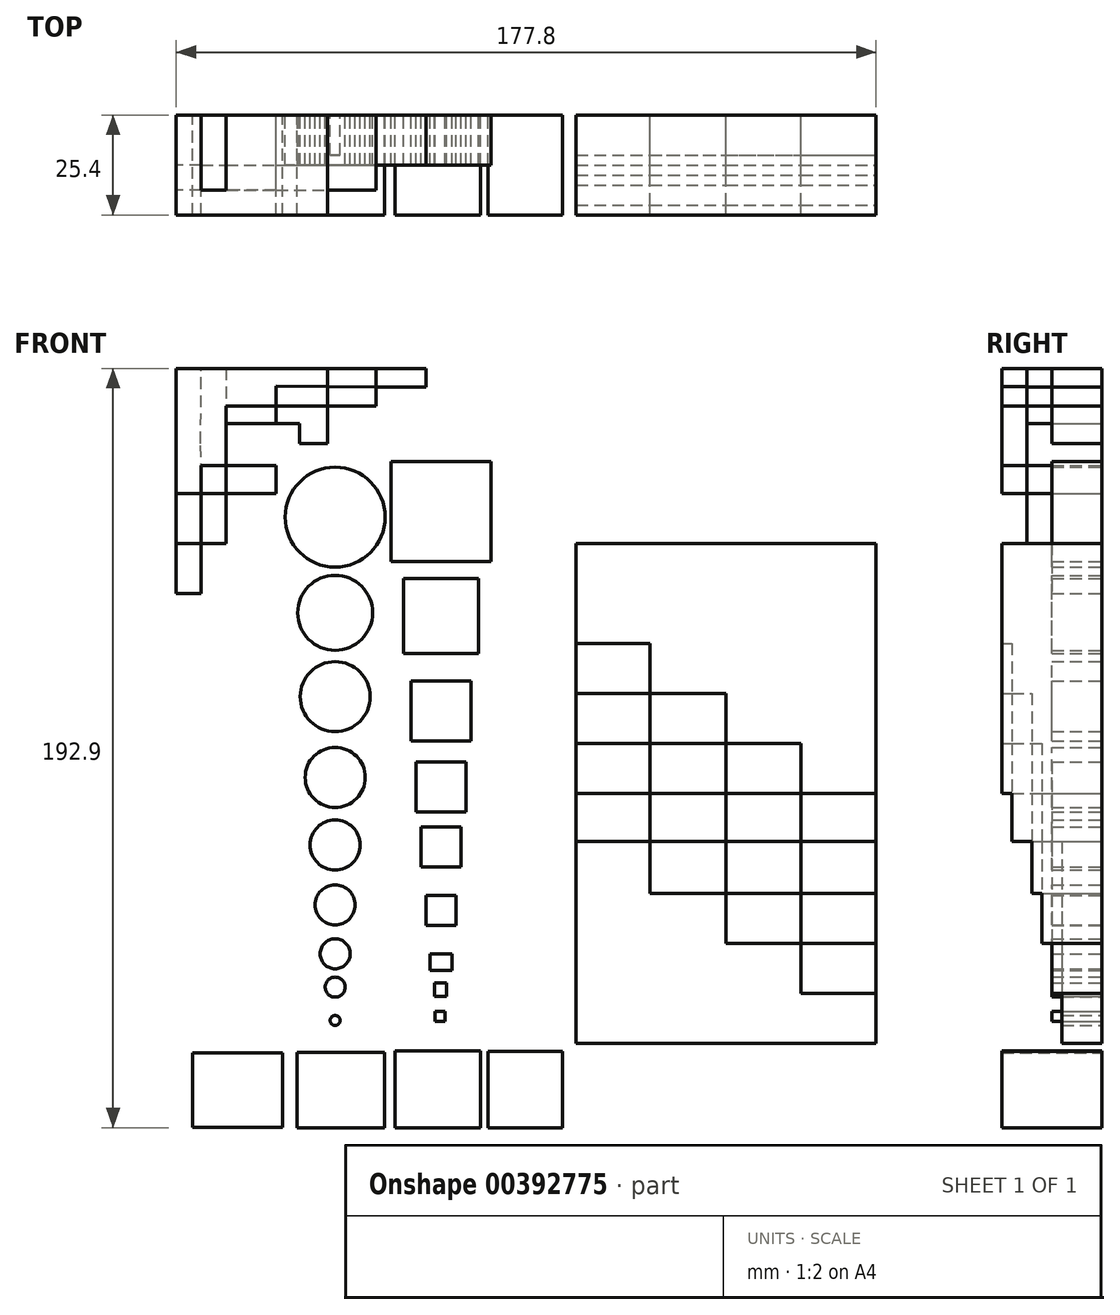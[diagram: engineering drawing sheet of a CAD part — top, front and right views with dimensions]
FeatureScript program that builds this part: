
annotation { "Feature Type Name" : "Feature", "Feature Type Description" : "" }
export const myFeature = defineFeature(function(context is Context, id is Id, definition is map)
    precondition{}
    {
        {
            var Q0;
            Q0=qCreatedBy(makeId("Front.planeOp"),FACE);
            var sketch = newSketch(context, id + "F0", { "sketchPlane" : qUnion([Q0])});
            skLineSegment(sketch, "E0.bottom", {"start": v(-139.7, 107.95) * mm, "end": v(139.7, 107.95) * mm});
            skLineSegment(sketch, "E0.top", {"start": v(-139.7, -107.95) * mm, "end": v(139.7, -107.95) * mm});
            skLineSegment(sketch, "E0.left", {"start": v(-139.7, 107.95) * mm, "end": v(-139.7, -107.95) * mm});
            skLineSegment(sketch, "E0.right", {"start": v(139.7, 107.95) * mm, "end": v(139.7, -107.95) * mm});
            skPoint(sketch, "E0.middle", {"position": v(0, 0) * mm});
            skLineSegment(sketch, "E1.bottom", {"start": v(-129.43, 76.2) * mm, "end": v(-104.03, 76.2) * mm});
            skLineSegment(sketch, "E1.top", {"start": v(-129.43, -76.2) * mm, "end": v(-104.03, -76.2) * mm});
            skLineSegment(sketch, "E1.left", {"start": v(-129.43, 76.2) * mm, "end": v(-129.43, -76.2) * mm});
            skLineSegment(sketch, "E1.right", {"start": v(-104.03, 76.2) * mm, "end": v(-104.03, -76.2) * mm});
            skLineSegment(sketch, "E2.bottom", {"start": v(-104.03, 76.2) * mm, "end": v(-27.83, 76.2) * mm});
            skLineSegment(sketch, "E2.top", {"start": v(-104.03, -76.2) * mm, "end": v(-27.83, -76.2) * mm});
            skLineSegment(sketch, "E2.right", {"start": v(-27.83, 76.2) * mm, "end": v(-27.83, -76.2) * mm});
            skLineSegment(sketch, "E3.bottom", {"start": v(-27.83, 76.2) * mm, "end": v(48.37, 76.2) * mm});
            skLineSegment(sketch, "E3.top", {"start": v(-27.83, -76.2) * mm, "end": v(48.37, -76.2) * mm});
            skLineSegment(sketch, "E3.right", {"start": v(48.37, 76.2) * mm, "end": v(48.37, -76.2) * mm});
            skPoint(sketch, "E4", {"position": v(-116.73, 76.2) * mm});
            skPoint(sketch, "E5", {"position": v(-116.73, -76.2) * mm});
            skLineSegment(sketch, "E6", {"start": v(-129.43, 0) * mm, "end": v(-116.57, 0) * mm});
            skPoint(sketch, "E6.startSnap0", {"position": v(-139.7, 0) * mm});
            skLineSegment(sketch, "E7", {"start": v(-116.73, -24.91) * mm, "end": v(-129.43, -24.91) * mm});
            skPoint(sketch, "E7.endSnap0", {"position": v(-129.43, 0) * mm});
            skLineSegment(sketch, "E8", {"start": v(-116.73, 50.8) * mm, "end": v(-129.43, 50.8) * mm});
            skLineSegment(sketch, "E9", {"start": v(-116.57, 25.4) * mm, "end": v(-129.43, 25.4) * mm});
            skLineSegment(sketch, "E10", {"start": v(-116.73, -50.8) * mm, "end": v(-129.43, -50.8) * mm});
            skPoint(sketch, "E11", {"position": v(-65.93, 76.2) * mm});
            skPoint(sketch, "E12", {"position": v(10.27, 76.2) * mm});
            skPoint(sketch, "E13", {"position": v(48.37, 0) * mm});
            skPoint(sketch, "E14", {"position": v(-65.93, -76.2) * mm});
            skPoint(sketch, "E15", {"position": v(10.27, -76.2) * mm});
            skPoint(sketch, "E16", {"position": v(10.27, 0) * mm});
            skPoint(sketch, "E17", {"position": v(-89.05, 76.2) * mm});
            skPoint(sketch, "E18", {"position": v(-62.1, 76.2) * mm});
            skPoint(sketch, "E19", {"position": v(-9.04, 76.2) * mm});
            skPoint(sketch, "E20", {"position": v(29.32, 76.2) * mm});
            skLineSegment(sketch, "E21.bottom", {"start": v(68.19, -99.33) * mm, "end": v(116.65, -99.33) * mm});
            skLineSegment(sketch, "E21.top", {"start": v(68.19, 67.86) * mm, "end": v(116.65, 67.86) * mm});
            skLineSegment(sketch, "E21.left", {"start": v(68.19, 67.86) * mm, "end": v(68.19, -99.33) * mm});
            skLineSegment(sketch, "E21.right", {"start": v(116.65, 67.86) * mm, "end": v(116.65, -99.33) * mm});
            skText(sketch, "E22", { "text": "Instructions", "fontName": "OpenSans-Regular.ttf"});
            skLineSegment(sketch, "E23", {"start": v(-123.08, 63.5) * mm, "end": v(-129.43, 63.5) * mm});
            skLineSegment(sketch, "E24", {"start": v(-129.43, 63.5) * mm, "end": v(-129.43, 50.8) * mm});
            skLineSegment(sketch, "E25", {"start": v(-129.43, 25.4) * mm, "end": v(-129.43, 38.1) * mm});
            skLineSegment(sketch, "E26", {"start": v(-129.43, 38.1) * mm, "end": v(-123.08, 38.1) * mm});
            skLineSegment(sketch, "E27", {"start": v(-123.08, 12.7) * mm, "end": v(-129.43, 12.7) * mm});
            skLineSegment(sketch, "E28", {"start": v(-129.43, 12.7) * mm, "end": v(-129.43, 0) * mm});
            skLineSegment(sketch, "E29", {"start": v(-123.08, -12.7) * mm, "end": v(-129.43, -12.7) * mm});
            skLineSegment(sketch, "E30", {"start": v(-129.43, -12.7) * mm, "end": v(-129.43, -24.91) * mm});
            skLineSegment(sketch, "E31", {"start": v(-123.08, -38.1) * mm, "end": v(-129.43, -38.1) * mm});
            skLineSegment(sketch, "E32", {"start": v(-129.43, -38.1) * mm, "end": v(-129.43, -50.8) * mm});
            skLineSegment(sketch, "E33", {"start": v(-123.08, -63.5) * mm, "end": v(-129.43, -63.5) * mm});
            skLineSegment(sketch, "E34", {"start": v(-129.43, -63.5) * mm, "end": v(-129.43, -76.2) * mm});
            skLineSegment(sketch, "E35.top", {"start": v(-27.83, 63.5) * mm, "end": v(48.37, 63.5) * mm});
            skLineSegment(sketch, "E35.left", {"start": v(-27.83, 76.2) * mm, "end": v(-27.83, 63.5) * mm});
            skLineSegment(sketch, "E35.right", {"start": v(48.37, 76.2) * mm, "end": v(48.37, 63.5) * mm});
            skLineSegment(sketch, "E36.bottom", {"start": v(-27.83, 63.5) * mm, "end": v(-9.04, 63.5) * mm});
            skLineSegment(sketch, "E36.top", {"start": v(-27.83, -76.2) * mm, "end": v(-9.04, -76.2) * mm});
            skLineSegment(sketch, "E36.left", {"start": v(-27.83, 63.5) * mm, "end": v(-27.83, -76.2) * mm});
            skLineSegment(sketch, "E36.right", {"start": v(-9.04, 63.5) * mm, "end": v(-9.04, -76.2) * mm});
            skLineSegment(sketch, "E37.bottom", {"start": v(-9.04, 63.5) * mm, "end": v(10.27, 63.5) * mm});
            skLineSegment(sketch, "E37.top", {"start": v(-9.04, -76.2) * mm, "end": v(10.27, -76.2) * mm});
            skLineSegment(sketch, "E37.right", {"start": v(10.27, 63.5) * mm, "end": v(10.27, -76.2) * mm});
            skLineSegment(sketch, "E38.bottom", {"start": v(10.27, 63.5) * mm, "end": v(29.32, 63.5) * mm});
            skLineSegment(sketch, "E38.top", {"start": v(10.27, -76.2) * mm, "end": v(29.32, -76.2) * mm});
            skLineSegment(sketch, "E38.right", {"start": v(29.32, 63.5) * mm, "end": v(29.32, -76.2) * mm});
            skLineSegment(sketch, "E39", {"start": v(-9.04, 76.2) * mm, "end": v(-9.04, 63.5) * mm});
            skLineSegment(sketch, "E40", {"start": v(10.27, 76.2) * mm, "end": v(10.27, 63.5) * mm});
            skLineSegment(sketch, "E41", {"start": v(29.32, 76.2) * mm, "end": v(29.32, 63.5) * mm});
            skPoint(sketch, "E42", {"position": v(-104.03, -63.5) * mm});
            skPoint(sketch, "E43", {"position": v(-104.03, -50.8) * mm});
            skPoint(sketch, "E44", {"position": v(-104.03, -38.1) * mm});
            skPoint(sketch, "E45", {"position": v(-104.03, -24.91) * mm});
            skPoint(sketch, "E46", {"position": v(-123.08, -12.7) * mm});
            skPoint(sketch, "E47", {"position": v(-104.03, -12.7) * mm});
            skPoint(sketch, "E48", {"position": v(-116.57, 0) * mm});
            skPoint(sketch, "E49", {"position": v(-104.03, 0) * mm});
            skPoint(sketch, "E50", {"position": v(-123.08, 12.7) * mm});
            skPoint(sketch, "E51", {"position": v(-104.03, 12.7) * mm});
            skPoint(sketch, "E52", {"position": v(-104.03, 25.4) * mm});
            skPoint(sketch, "E53", {"position": v(-104.03, 38.1) * mm});
            skPoint(sketch, "E54", {"position": v(-104.03, 50.8) * mm});
            skPoint(sketch, "E55", {"position": v(-104.03, 63.5) * mm});
            skPoint(sketch, "E56", {"position": v(-27.83, 50.8) * mm});
            skPoint(sketch, "E57", {"position": v(-27.83, 38.1) * mm});
            skPoint(sketch, "E58", {"position": v(-27.83, 25.4) * mm});
            skPoint(sketch, "E59", {"position": v(-27.83, 12.7) * mm});
            skPoint(sketch, "E60", {"position": v(-27.83, 0) * mm});
            skPoint(sketch, "E61", {"position": v(-27.83, -12.7) * mm});
            skPoint(sketch, "E62", {"position": v(-27.83, -24.91) * mm});
            skPoint(sketch, "E63", {"position": v(-27.83, -38.1) * mm});
            skPoint(sketch, "E64", {"position": v(-27.83, -50.8) * mm});
            skPoint(sketch, "E65", {"position": v(-27.83, -63.5) * mm});
            skPoint(sketch, "E66", {"position": v(-9.04, 50.8) * mm});
            skPoint(sketch, "E67", {"position": v(-9.04, 38.1) * mm});
            skPoint(sketch, "E68", {"position": v(10.27, 38.1) * mm});
            skPoint(sketch, "E69", {"position": v(29.32, 38.1) * mm});
            skPoint(sketch, "E70", {"position": v(48.37, 38.1) * mm});
            skPoint(sketch, "E71", {"position": v(29.32, 50.8) * mm});
            skPoint(sketch, "E72", {"position": v(10.27, 50.8) * mm});
            skPoint(sketch, "E73", {"position": v(48.37, 50.8) * mm});
            skPoint(sketch, "E74", {"position": v(-9.04, 25.4) * mm});
            skPoint(sketch, "E75", {"position": v(10.27, 25.4) * mm});
            skPoint(sketch, "E76", {"position": v(29.32, 25.4) * mm});
            skPoint(sketch, "E77", {"position": v(48.37, 25.4) * mm});
            skPoint(sketch, "E78", {"position": v(-9.04, 12.7) * mm});
            skPoint(sketch, "E79", {"position": v(10.27, 12.7) * mm});
            skPoint(sketch, "E80", {"position": v(-8.78, 0) * mm});
            skPoint(sketch, "E81", {"position": v(-9.04, -12.7) * mm});
            skPoint(sketch, "E82", {"position": v(-9.04, -24.91) * mm});
            skPoint(sketch, "E83", {"position": v(-9.04, -38.1) * mm});
            skPoint(sketch, "E84", {"position": v(-9.04, -50.8) * mm});
            skPoint(sketch, "E85", {"position": v(-9.04, -63.5) * mm});
            skPoint(sketch, "E86", {"position": v(10.27, -63.5) * mm});
            skPoint(sketch, "E87", {"position": v(29.32, -63.5) * mm});
            skPoint(sketch, "E88", {"position": v(48.37, -63.5) * mm});
            skPoint(sketch, "E89", {"position": v(48.37, -50.8) * mm});
            skPoint(sketch, "E90", {"position": v(29.32, -50.8) * mm});
            skPoint(sketch, "E91", {"position": v(10.27, -50.8) * mm});
            skPoint(sketch, "E92", {"position": v(10.27, -38.1) * mm});
            skPoint(sketch, "E93", {"position": v(29.32, -38.1) * mm});
            skPoint(sketch, "E94", {"position": v(48.37, -38.1) * mm});
            skPoint(sketch, "E95", {"position": v(48.37, -24.91) * mm});
            skPoint(sketch, "E96", {"position": v(29.32, -24.91) * mm});
            skPoint(sketch, "E97", {"position": v(10.27, -24.91) * mm});
            skPoint(sketch, "E98", {"position": v(10.27, -12.7) * mm});
            skPoint(sketch, "E99", {"position": v(29.32, -12.7) * mm});
            skPoint(sketch, "E100", {"position": v(48.37, -12.7) * mm});
            skPoint(sketch, "E101", {"position": v(48.37, 12.7) * mm});
            skPoint(sketch, "E102", {"position": v(29.32, 12.7) * mm});
            skPoint(sketch, "E103", {"position": v(29.32, 0) * mm});
            skCircle(sketch, "E104", {"center": v(-89.05, 57.46) * mm, "radius": 12.7 * mm});
            skCircle(sketch, "E105", {"center": v(-89.05, 33.17) * mm, "radius": 9.53 * mm});
            skCircle(sketch, "E106", {"center": v(-89.05, -8.65) * mm, "radius": 7.62 * mm});
            skCircle(sketch, "E107", {"center": v(-89.05, -25.83) * mm, "radius": 6.35 * mm});
            skCircle(sketch, "E108", {"center": v(-89.05, -41.03) * mm, "radius": 5.08 * mm});
            skCircle(sketch, "E109", {"center": v(-89.05, -53.47) * mm, "radius": 3.81 * mm});
            skCircle(sketch, "E110", {"center": v(-89.05, -61.94) * mm, "radius": 2.54 * mm});
            skCircle(sketch, "E111", {"center": v(-89.05, -70.41) * mm, "radius": 1.27 * mm});
            skCircle(sketch, "E112", {"center": v(-89.05, 11.86) * mm, "radius": 8.9 * mm});
            skLineSegment(sketch, "E113", {"start": v(-27.83, -24.91) * mm, "end": v(-9.04, -24.91) * mm});
            skLineSegment(sketch, "E114", {"start": v(-9.04, -38.1) * mm, "end": v(10.27, -38.1) * mm});
            skLineSegment(sketch, "E115", {"start": v(10.27, -50.8) * mm, "end": v(29.32, -50.8) * mm});
            skLineSegment(sketch, "E116", {"start": v(29.32, -63.5) * mm, "end": v(48.37, -63.5) * mm});
            skLineSegment(sketch, "E117.bottom", {"start": v(-64.92, -53.52) * mm, "end": v(-59.3, -53.52) * mm});
            skLineSegment(sketch, "E117.top", {"start": v(-64.92, -57.7) * mm, "end": v(-59.3, -57.7) * mm});
            skLineSegment(sketch, "E117.left", {"start": v(-64.92, -53.52) * mm, "end": v(-64.92, -57.7) * mm});
            skLineSegment(sketch, "E117.right", {"start": v(-59.3, -53.52) * mm, "end": v(-59.3, -57.7) * mm});
            skPoint(sketch, "E117.middle", {"position": v(-62.1, -55.6) * mm});
            skLineSegment(sketch, "E118.bottom", {"start": v(-63.7, -68.11) * mm, "end": v(-61.16, -68.11) * mm});
            skLineSegment(sketch, "E118.top", {"start": v(-63.7, -70.65) * mm, "end": v(-61.16, -70.65) * mm});
            skLineSegment(sketch, "E118.left", {"start": v(-63.7, -68.11) * mm, "end": v(-63.7, -70.65) * mm});
            skLineSegment(sketch, "E118.right", {"start": v(-61.16, -68.11) * mm, "end": v(-61.16, -70.65) * mm});
            skPoint(sketch, "E118.middle", {"position": v(-62.43, -69.38) * mm});
            skLineSegment(sketch, "E119.bottom", {"start": v(48.37, -76.2) * mm, "end": v(-129.43, -76.2) * mm});
            skLineSegment(sketch, "E119.top", {"start": v(48.37, -100.6) * mm, "end": v(-129.43, -100.6) * mm});
            skLineSegment(sketch, "E119.left", {"start": v(48.37, -76.2) * mm, "end": v(48.37, -100.6) * mm});
            skLineSegment(sketch, "E119.right", {"start": v(-129.43, -76.2) * mm, "end": v(-129.43, -100.6) * mm});
            skLineSegment(sketch, "E120.top", {"start": v(-27.83, -100.6) * mm, "end": v(-9.04, -100.6) * mm});
            skLineSegment(sketch, "E120.left", {"start": v(-27.83, -76.2) * mm, "end": v(-27.83, -100.6) * mm});
            skLineSegment(sketch, "E120.right", {"start": v(-9.04, -76.2) * mm, "end": v(-9.04, -100.6) * mm});
            skLineSegment(sketch, "E121.top", {"start": v(10.27, -100.6) * mm, "end": v(29.32, -100.6) * mm});
            skLineSegment(sketch, "E121.left", {"start": v(10.27, -76.2) * mm, "end": v(10.27, -100.6) * mm});
            skLineSegment(sketch, "E121.right", {"start": v(29.32, -76.2) * mm, "end": v(29.32, -100.6) * mm});
            skLineSegment(sketch, "E122", {"start": v(-27.83, 25.4) * mm, "end": v(-9.04, 25.4) * mm});
            skLineSegment(sketch, "E123", {"start": v(-9.04, 12.7) * mm, "end": v(10.27, 12.7) * mm});
            skLineSegment(sketch, "E124", {"start": v(10.27, 0) * mm, "end": v(29.32, 0) * mm});
            skLineSegment(sketch, "E125", {"start": v(29.32, -12.7) * mm, "end": v(48.37, -12.7) * mm});
            skLineSegment(sketch, "E126", {"start": v(-27.83, 12.7) * mm, "end": v(-9.04, 12.7) * mm});
            skLineSegment(sketch, "E127", {"start": v(-8.78, 0) * mm, "end": v(10.27, 0) * mm});
            skLineSegment(sketch, "E128", {"start": v(10.27, -12.7) * mm, "end": v(29.32, -12.7) * mm});
            skLineSegment(sketch, "E129", {"start": v(-27.83, 0) * mm, "end": v(-8.78, 0) * mm});
            skLineSegment(sketch, "E130", {"start": v(-27.83, -12.7) * mm, "end": v(-9.04, -12.7) * mm});
            skLineSegment(sketch, "E131", {"start": v(-9.04, -12.7) * mm, "end": v(10.27, -12.7) * mm});
            skLineSegment(sketch, "E132", {"start": v(10.27, -38.1) * mm, "end": v(29.32, -38.1) * mm});
            skLineSegment(sketch, "E133", {"start": v(29.32, -38.1) * mm, "end": v(48.37, -38.1) * mm});
            skLineSegment(sketch, "E134", {"start": v(29.32, -50.8) * mm, "end": v(48.37, -50.8) * mm});
            skLineSegment(sketch, "E135", {"start": v(-9.04, -24.91) * mm, "end": v(10.27, -24.91) * mm});
            skLineSegment(sketch, "E136", {"start": v(10.27, -24.91) * mm, "end": v(29.32, -24.91) * mm});
            skLineSegment(sketch, "E137", {"start": v(29.32, -24.91) * mm, "end": v(48.37, -24.91) * mm});
            skLineSegment(sketch, "E138", {"start": v(-27.83, 50.8) * mm, "end": v(48.37, 50.8) * mm});
            skLineSegment(sketch, "E139.bottom", {"start": v(-49.4, 46.22) * mm, "end": v(-74.8, 46.22) * mm});
            skLineSegment(sketch, "E139.top", {"start": v(-49.4, 71.62) * mm, "end": v(-74.8, 71.62) * mm});
            skLineSegment(sketch, "E139.left", {"start": v(-49.4, 46.22) * mm, "end": v(-49.4, 71.62) * mm});
            skLineSegment(sketch, "E139.right", {"start": v(-74.8, 46.22) * mm, "end": v(-74.8, 71.62) * mm});
            skPoint(sketch, "E139.middle", {"position": v(-62.1, 58.92) * mm});
            skLineSegment(sketch, "E140.bottom", {"start": v(-52.58, 22.78) * mm, "end": v(-71.63, 22.78) * mm});
            skLineSegment(sketch, "E140.top", {"start": v(-52.58, 41.83) * mm, "end": v(-71.63, 41.83) * mm});
            skLineSegment(sketch, "E140.left", {"start": v(-52.58, 22.78) * mm, "end": v(-52.58, 41.83) * mm});
            skLineSegment(sketch, "E140.right", {"start": v(-71.63, 22.78) * mm, "end": v(-71.63, 41.83) * mm});
            skPoint(sketch, "E140.middle", {"position": v(-62.1, 32.3) * mm});
            skLineSegment(sketch, "E141.bottom", {"start": v(-54.49, 0.58) * mm, "end": v(-69.73, 0.58) * mm});
            skLineSegment(sketch, "E141.top", {"start": v(-54.49, 15.82) * mm, "end": v(-69.73, 15.82) * mm});
            skLineSegment(sketch, "E141.left", {"start": v(-54.49, 0.58) * mm, "end": v(-54.49, 15.82) * mm});
            skLineSegment(sketch, "E141.right", {"start": v(-69.73, 0.58) * mm, "end": v(-69.73, 15.82) * mm});
            skPoint(sketch, "E141.middle", {"position": v(-62.1, 8.2) * mm});
            skLineSegment(sketch, "E142.bottom", {"start": v(-65.92, -38.58) * mm, "end": v(-58.3, -38.58) * mm});
            skLineSegment(sketch, "E142.top", {"start": v(-65.92, -46.2) * mm, "end": v(-58.3, -46.2) * mm});
            skLineSegment(sketch, "E142.left", {"start": v(-65.92, -38.58) * mm, "end": v(-65.92, -46.2) * mm});
            skLineSegment(sketch, "E142.right", {"start": v(-58.3, -38.58) * mm, "end": v(-58.3, -46.2) * mm});
            skPoint(sketch, "E142.middle", {"position": v(-62.1, -42.4) * mm});
            skLineSegment(sketch, "E143.bottom", {"start": v(-67.19, -21.2) * mm, "end": v(-57.03, -21.2) * mm});
            skLineSegment(sketch, "E143.top", {"start": v(-67.19, -31.35) * mm, "end": v(-57.03, -31.35) * mm});
            skLineSegment(sketch, "E143.left", {"start": v(-67.19, -21.2) * mm, "end": v(-67.19, -31.35) * mm});
            skLineSegment(sketch, "E143.right", {"start": v(-57.03, -21.2) * mm, "end": v(-57.03, -31.35) * mm});
            skPoint(sketch, "E143.middle", {"position": v(-62.1, -26.27) * mm});
            skLineSegment(sketch, "E144.bottom", {"start": v(-68.46, -4.78) * mm, "end": v(-55.76, -4.78) * mm});
            skLineSegment(sketch, "E144.top", {"start": v(-68.46, -17.48) * mm, "end": v(-55.76, -17.48) * mm});
            skLineSegment(sketch, "E144.left", {"start": v(-68.46, -4.78) * mm, "end": v(-68.46, -17.48) * mm});
            skLineSegment(sketch, "E144.right", {"start": v(-55.76, -4.78) * mm, "end": v(-55.76, -17.48) * mm});
            skPoint(sketch, "E144.middle", {"position": v(-62.1, -11.13) * mm});
            skLineSegment(sketch, "E145.bottom", {"start": v(-60.78, -64.35) * mm, "end": v(-63.79, -64.35) * mm});
            skLineSegment(sketch, "E145.top", {"start": v(-60.78, -60.9) * mm, "end": v(-63.79, -60.9) * mm});
            skLineSegment(sketch, "E145.left", {"start": v(-60.78, -64.35) * mm, "end": v(-60.78, -60.9) * mm});
            skLineSegment(sketch, "E145.right", {"start": v(-63.79, -64.35) * mm, "end": v(-63.79, -60.9) * mm});
            skPoint(sketch, "E145.middle", {"position": v(-62.28, -62.62) * mm});
            skLineSegment(sketch, "E146.bottom", {"start": v(-129.43, 76.2) * mm, "end": v(48.37, 76.2) * mm});
            skLineSegment(sketch, "E146.top", {"start": v(-129.43, 95.25) * mm, "end": v(48.37, 95.25) * mm});
            skLineSegment(sketch, "E146.left", {"start": v(-129.43, 76.2) * mm, "end": v(-129.43, 95.25) * mm});
            skLineSegment(sketch, "E146.right", {"start": v(48.37, 76.2) * mm, "end": v(48.37, 95.25) * mm});
            skPoint(sketch, "E147", {"position": v(-104.03, 95.25) * mm});
            skPoint(sketch, "E148", {"position": v(-89.05, 95.25) * mm});
            skPoint(sketch, "E149", {"position": v(-27.83, 95.25) * mm});
            skPoint(sketch, "E150", {"position": v(-9.04, 95.25) * mm});
            skPoint(sketch, "E151", {"position": v(10.27, 95.25) * mm});
            skPoint(sketch, "E152", {"position": v(29.32, 95.25) * mm});
            skPoint(sketch, "E153", {"position": v(-46.03, 95.25) * mm});
            skPoint(sketch, "E154", {"position": v(-116.73, 95.25) * mm});
            skPoint(sketch, "E155", {"position": v(-129.43, 85.72) * mm});
            skPoint(sketch, "E156", {"position": v(48.37, 85.72) * mm});
            skLineSegment(sketch, "E157", {"start": v(-104.03, 95.25) * mm, "end": v(-104.03, 85.72) * mm});
            skPoint(sketch, "E158", {"position": v(-76.14, 95.25) * mm});
            skPoint(sketch, "E159", {"position": v(-210.78, 24.73) * mm});
            skLineSegment(sketch, "E160.1.0.0", {"start": v(-78.63, 95.25) * mm, "end": v(-78.63, 85.72) * mm});
            skLineSegment(sketch, "E160.2.0.0", {"start": v(-53.23, 95.25) * mm, "end": v(-53.23, 85.72) * mm});
            skLineSegment(sketch, "E160.3.0.0", {"start": v(-27.83, 95.25) * mm, "end": v(-27.83, 85.72) * mm});
            skLineSegment(sketch, "E160.4.0.0", {"start": v(-2.43, 95.25) * mm, "end": v(-2.43, 85.72) * mm});
            skLineSegment(sketch, "E160.5.0.0", {"start": v(22.97, 95.25) * mm, "end": v(22.97, 85.72) * mm});
            skLineSegment(sketch, "E160.direction1", {"start": v(-104.03, 85.72) * mm, "end": v(-78.63, 85.72) * mm, "construction": true});
            skLineSegment(sketch, "E161", {"start": v(-129.43, 85.72) * mm, "end": v(-78.63, 85.72) * mm});
            skLineSegment(sketch, "E162", {"start": v(-123.08, 63.5) * mm, "end": v(-104.03, 63.5) * mm});
            skLineSegment(sketch, "E163", {"start": v(-103.97, 75.58) * mm, "end": v(-104.03, 85.72) * mm});
            skLineSegment(sketch, "E164", {"start": v(-116.73, 95.25) * mm, "end": v(-116.73, 63.5) * mm});
            skPoint(sketch, "E165", {"position": v(-123.13, 95.25) * mm});
            skPoint(sketch, "E166", {"position": v(-110.36, 95.25) * mm});
            skPoint(sketch, "E167", {"position": v(-96.53, 95.25) * mm});
            skPoint(sketch, "E168", {"position": v(-123.2, 76.2) * mm});
            skPoint(sketch, "E169", {"position": v(-110.3, 76.2) * mm});
            skPoint(sketch, "E170", {"position": v(-129.43, 90.76) * mm});
            skPoint(sketch, "E171", {"position": v(-129.43, 81.3) * mm});
            skLineSegment(sketch, "E172", {"start": v(-129.43, 90.76) * mm, "end": v(-104.03, 90.76) * mm});
            skLineSegment(sketch, "E173", {"start": v(-104, 81.3) * mm, "end": v(-129.43, 81.3) * mm});
            skLineSegment(sketch, "E174", {"start": v(-123.2, 76.2) * mm, "end": v(-123.13, 95.25) * mm});
            skLineSegment(sketch, "E175", {"start": v(-123.08, 63.5) * mm, "end": v(-123.2, 76.2) * mm});
            skLineSegment(sketch, "E176", {"start": v(-110.36, 95.25) * mm, "end": v(-110.36, 63.5) * mm});
            skLineSegment(sketch, "E177", {"start": v(-116.73, 50.8) * mm, "end": v(-116.73, 63.5) * mm});
            skLineSegment(sketch, "E178", {"start": v(-123.08, 63.5) * mm, "end": v(-123.08, 38.1) * mm});
            skLineSegment(sketch, "E179", {"start": v(-104.03, 90.76) * mm, "end": v(-65.99, 90.49) * mm});
            skPoint(sketch, "E179.endSnap0", {"position": v(-78.63, 90.49) * mm});
            skLineSegment(sketch, "E180", {"start": v(-91, 95.25) * mm, "end": v(-91, 85.72) * mm});
            skLineSegment(sketch, "E181", {"start": v(-98, 95.25) * mm, "end": v(-98, 85.72) * mm});
            skLineSegment(sketch, "E182", {"start": v(-98.14, 76.2) * mm, "end": v(-98, 85.72) * mm});
            skLineSegment(sketch, "E183", {"start": v(-104, 81.3) * mm, "end": v(-98, 81.27) * mm});
            skLineSegment(sketch, "E184", {"start": v(-65.99, 90.49) * mm, "end": v(-65.99, 95.25) * mm});
            skLineSegment(sketch, "E185", {"start": v(-84.93, 95.25) * mm, "end": v(-84.93, 85.72) * mm});
            skLineSegment(sketch, "E186", {"start": v(-129.43, 70.6) * mm, "end": v(-104.03, 70.6) * mm});
            skLineSegment(sketch, "E187", {"start": v(-129.43, 57.15) * mm, "end": v(-116.73, 57.15) * mm});
            skLineSegment(sketch, "E188", {"start": v(-129.43, 45.08) * mm, "end": v(-123.08, 45.08) * mm});
            skLineSegment(sketch, "E189", {"start": v(-72.6, 95.25) * mm, "end": v(-72.6, 90.53) * mm});
            skLineSegment(sketch, "E190", {"start": v(-91, 85.72) * mm, "end": v(-91, 76.2) * mm});
            skLineSegment(sketch, "E191", {"start": v(-98, 81.27) * mm, "end": v(-91, 81.27) * mm});
            skLineSegment(sketch, "E192.bottom", {"start": v(-125.23, -78.61) * mm, "end": v(-102.43, -78.61) * mm});
            skLineSegment(sketch, "E192.top", {"start": v(-125.23, -97.54) * mm, "end": v(-102.43, -97.54) * mm});
            skLineSegment(sketch, "E192.left", {"start": v(-125.23, -78.61) * mm, "end": v(-125.23, -97.54) * mm});
            skLineSegment(sketch, "E192.right", {"start": v(-102.43, -78.61) * mm, "end": v(-102.43, -97.54) * mm});
            skLineSegment(sketch, "E193.bottom", {"start": v(-98.75, -78.48) * mm, "end": v(-76.5, -78.48) * mm});
            skLineSegment(sketch, "E193.top", {"start": v(-98.75, -97.65) * mm, "end": v(-76.5, -97.65) * mm});
            skLineSegment(sketch, "E193.left", {"start": v(-98.75, -78.48) * mm, "end": v(-98.75, -97.65) * mm});
            skLineSegment(sketch, "E193.right", {"start": v(-76.5, -78.48) * mm, "end": v(-76.5, -97.65) * mm});
            skLineSegment(sketch, "E194.bottom", {"start": v(-73.79, -78.12) * mm, "end": v(-52.09, -78.12) * mm});
            skLineSegment(sketch, "E194.top", {"start": v(-73.79, -97.65) * mm, "end": v(-52.09, -97.65) * mm});
            skLineSegment(sketch, "E194.left", {"start": v(-73.79, -78.12) * mm, "end": v(-73.79, -97.65) * mm});
            skLineSegment(sketch, "E194.right", {"start": v(-52.09, -78.12) * mm, "end": v(-52.09, -97.65) * mm});
            skLineSegment(sketch, "E195.bottom", {"start": v(-50.28, -78.3) * mm, "end": v(-31.29, -78.3) * mm});
            skLineSegment(sketch, "E195.top", {"start": v(-50.28, -97.65) * mm, "end": v(-31.29, -97.65) * mm});
            skLineSegment(sketch, "E195.left", {"start": v(-50.28, -78.3) * mm, "end": v(-50.28, -97.65) * mm});
            skLineSegment(sketch, "E195.right", {"start": v(-31.29, -78.3) * mm, "end": v(-31.29, -97.65) * mm});
            skPoint(sketch, "E196", {"position": v(-22.97, -18.6) * mm});
            skPoint(sketch, "E197", {"position": v(-15.04, -19.37) * mm});
            skPoint(sketch, "E198", {"position": v(-2.5, -16.82) * mm});
            skPoint(sketch, "E199", {"position": v(4.15, -19.89) * mm});
            skPoint(sketch, "E200", {"position": v(20, -16.56) * mm});
            skPoint(sketch, "E201", {"position": v(14.89, -20.4) * mm});
            skPoint(sketch, "E202", {"position": v(40.98, -17.33) * mm});
            skPoint(sketch, "E203", {"position": v(35.6, -19.63) * mm});
            skPoint(sketch, "E204", {"position": v(0.82, -31.9) * mm});
            skPoint(sketch, "E205", {"position": v(20.52, -31.14) * mm});
            skPoint(sketch, "E206", {"position": v(43.54, -33.95) * mm});
            skPoint(sketch, "E207", {"position": v(-19.9, -30.63) * mm});
            skPoint(sketch, "E208", {"position": v(-24.02, -3.73) * mm});
            skPoint(sketch, "E209", {"position": v(-13.7, -3.52) * mm});
            skPoint(sketch, "E210", {"position": v(-21.44, -8.9) * mm});
            skPoint(sketch, "E211", {"position": v(-4.87, -3.95) * mm});
            skPoint(sketch, "E212", {"position": v(5.88, -5.45) * mm});
            skPoint(sketch, "E213", {"position": v(-3.8, -10.61) * mm});
            skPoint(sketch, "E214", {"position": v(15.56, -4.38) * mm});
            skPoint(sketch, "E215", {"position": v(24.8, -3.3) * mm});
            skPoint(sketch, "E216", {"position": v(24.8, -7.39) * mm});
            skPoint(sketch, "E217", {"position": v(36.85, -0.72) * mm});
            skPoint(sketch, "E218", {"position": v(40.72, -6.74) * mm});
            skPoint(sketch, "E219", {"position": v(34.27, -8.9) * mm});
            skPoint(sketch, "E220", {"position": v(-25.95, 9.39) * mm});
            skPoint(sketch, "E221", {"position": v(-12.83, 9.17) * mm});
            skPoint(sketch, "E222", {"position": v(-18.85, 7.88) * mm});
            skPoint(sketch, "E223", {"position": v(-15.84, 2.3) * mm});
            skPoint(sketch, "E224", {"position": v(-4.01, 10.47) * mm});
            skPoint(sketch, "E225", {"position": v(6.53, 9.17) * mm});
            skPoint(sketch, "E226", {"position": v(2.87, 3.8) * mm});
            skPoint(sketch, "E227", {"position": v(-3.15, 4.87) * mm});
            skPoint(sketch, "E228", {"position": v(15.34, 9.17) * mm});
            skPoint(sketch, "E229", {"position": v(25.02, 9.17) * mm});
            skPoint(sketch, "E230", {"position": v(23.73, 3.58) * mm});
            skPoint(sketch, "E231", {"position": v(16.2, 4.01) * mm});
            skPoint(sketch, "E232", {"position": v(33.2, 6.16) * mm});
            skPoint(sketch, "E233", {"position": v(38.79, 11.54) * mm});
            skPoint(sketch, "E234", {"position": v(45.46, 7.02) * mm});
            skPoint(sketch, "E235", {"position": v(40.5, 4.01) * mm});
            skPoint(sketch, "E236", {"position": v(-24.76, 19.13) * mm});
            skPoint(sketch, "E237", {"position": v(-20.92, 21.94) * mm});
            skPoint(sketch, "E238", {"position": v(-13, 22.2) * mm});
            skPoint(sketch, "E239", {"position": v(-13.5, 15.8) * mm});
            skPoint(sketch, "E240", {"position": v(-19.64, 17.09) * mm});
            skPoint(sketch, "E241", {"position": v(-5.83, 20.67) * mm});
            skPoint(sketch, "E242", {"position": v(-0.2, 23.74) * mm});
            skPoint(sketch, "E243", {"position": v(6.45, 21.94) * mm});
            skPoint(sketch, "E244", {"position": v(6.45, 17.6) * mm});
            skPoint(sketch, "E245", {"position": v(-0.46, 19.13) * mm});
            skPoint(sketch, "E246", {"position": v(13.6, 16.06) * mm});
            skPoint(sketch, "E247", {"position": v(21.02, 14.02) * mm});
            skPoint(sketch, "E248", {"position": v(25.37, 18.1) * mm});
            skPoint(sketch, "E249", {"position": v(24.6, 23.74) * mm});
            skPoint(sketch, "E250", {"position": v(15.14, 22.46) * mm});
            skPoint(sketch, "E251", {"position": v(33.05, 23.74) * mm});
            skPoint(sketch, "E252", {"position": v(33.81, 15.04) * mm});
            skPoint(sketch, "E253", {"position": v(37.65, 19.9) * mm});
            skPoint(sketch, "E254", {"position": v(44.56, 23.22) * mm});
            skPoint(sketch, "E255", {"position": v(43.79, 15.04) * mm});
            skText(sketch, "E256", { "text": "D", "fontName": "OpenSans-Regular.ttf"});
            skText(sketch, "E257", { "text": "C", "fontName": "OpenSans-Regular.ttf"});
            skText(sketch, "E258", { "text": "B", "fontName": "OpenSans-Regular.ttf"});
            skText(sketch, "E259", { "text": "A", "fontName": "OpenSans-Regular.ttf"});
            skLineSegment(sketch, "E260.bottom", {"start": v(68.19, 73.52) * mm, "end": v(116.65, 73.52) * mm});
            skLineSegment(sketch, "E260.left", {"start": v(68.19, 73.52) * mm, "end": v(68.19, 67.86) * mm});
            skLineSegment(sketch, "E260.right", {"start": v(116.65, 73.52) * mm, "end": v(116.65, 67.86) * mm});
            skText(sketch, "E261", { "text": "Location\nDiscoloration\nScratches\nNicks/Dings\nPin Holes\nSpecs", "fontName": "OpenSans-Regular.ttf"});
            skLineSegment(sketch, "E262", {"start": v(-38.73, 46.16) * mm, "end": v(-38.73, 72.32) * mm});
            skLineSegment(sketch, "E263", {"start": v(-38.73, 41.9) * mm, "end": v(-38.73, 22.74) * mm});
            skLineSegment(sketch, "E264", {"start": v(-39.34, 16.35) * mm, "end": v(-39.34, 0.84) * mm});
            skLineSegment(sketch, "E265", {"start": v(-38.73, -4.78) * mm, "end": v(-38.73, -18.6) * mm});
            skPoint(sketch, "E265.startSnap0", {"position": v(-62.1, -4.78) * mm});
            skLineSegment(sketch, "E266", {"start": v(-38.73, -21.97) * mm, "end": v(-38.73, -30.8) * mm});
            skLineSegment(sketch, "E267", {"start": v(-38.73, -37.35) * mm, "end": v(-38.73, -46.75) * mm});
            skLineSegment(sketch, "E268", {"start": v(-38.99, -52.18) * mm, "end": v(-38.99, -58.33) * mm});
            skLineSegment(sketch, "E269", {"start": v(-38.99, -61.22) * mm, "end": v(-38.99, -64.72) * mm});
            skLineSegment(sketch, "E270", {"start": v(-39.14, -67.46) * mm, "end": v(-39.14, -70.95) * mm});
            const initialGuessF0  = {"E22": [0.06852, 0.08904, 1, 0, 0.00743], "E256": [-0.0227, 0.06572, 1, 0, 0.0079], "E257": [-0.00324, 0.06591, 1, 0, 0.0076], "E258": [0.01613, 0.06575, 1, 0, 0.0076], "E259": [0.03432, 0.06509, 1, 0, 0.00977], "E261": [0.06819, 0.06786, 1, 0, 0.00566]};
            skSetInitialGuess(sketch, initialGuessF0);
            skSolve(sketch);
        }
        {
            var Q0;
            {var subQ4=sQuery(id+"F0.wireOp",EDGE,"E113");Q0=makeQuery(id+"F0.imprint","IMPRINT",FACE,{"disambiguationData":[TD([[makeQuery(id+"F0.imprint","IMPRINT",EDGE,{"derivedFrom":subQ4}),-1.0]])]});}
            var Q1;
            {var subQ4=sQuery(id+"F0.wireOp",EDGE,"E114");Q1=makeQuery(id+"F0.imprint","IMPRINT",FACE,{"disambiguationData":[TD([[makeQuery(id+"F0.imprint","IMPRINT",EDGE,{"derivedFrom":subQ4}),-1.0]])]});}
            var Q2;
            {var subQ0=sQuery(id+"F0.wireOp",EDGE,"E115");Q2=makeQuery(id+"F0.imprint","IMPRINT",FACE,{"disambiguationData":[TD([[makeQuery(id+"F0.imprint","IMPRINT",EDGE,{"derivedFrom":subQ0}),-1.0]])]});}
            var Q3;
            {var subQ3=sQuery(id+"F0.wireOp",EDGE,"E116");Q3=makeQuery(id+"F0.imprint","IMPRINT",FACE,{"disambiguationData":[TD([[makeQuery(id+"F0.imprint","IMPRINT",EDGE,{"derivedFrom":subQ3}),-1.0]])]});}
            var Q4;
            Q4=makeQuery(id+"F0.imprint","IMPRINT",FACE,{"disambiguationData":[TD([[makeQuery(id+"F0.imprint","IMPRINT",EDGE,{"derivedFrom":sQuery(id+"F0.wireOp",EDGE,"E111")}),1.0]])]});
            extrude(context, id + "F1", {"entities" : qUnion([Q0, Q1, Q2, Q3, Q4]), "depth" : 10.16 * mm});
        }
        {
            var Q0;
            {var subQ0=sQuery(id+"F0.wireOp",EDGE,"E122");Q0=makeQuery(id+"F0.imprint","IMPRINT",FACE,{"disambiguationData":[TD([[makeQuery(id+"F0.imprint","IMPRINT",EDGE,{"derivedFrom":subQ0}),1.0]])]});}
            var Q1;
            {var subQ0=sQuery(id+"F0.wireOp",EDGE,"E123");Q1=makeQuery(id+"F0.imprint","IMPRINT",FACE,{"disambiguationData":[TD([[makeQuery(id+"F0.imprint","IMPRINT",EDGE,{"derivedFrom":subQ0}),1.0]])]});}
            var Q2;
            {var subQ0=sQuery(id+"F0.wireOp",EDGE,"E124");Q2=makeQuery(id+"F0.imprint","IMPRINT",FACE,{"disambiguationData":[TD([[makeQuery(id+"F0.imprint","IMPRINT",EDGE,{"derivedFrom":subQ0}),1.0]])]});}
            var Q3;
            {var subQ0=sQuery(id+"F0.wireOp",EDGE,"E125");Q3=makeQuery(id+"F0.imprint","IMPRINT",FACE,{"disambiguationData":[TD([[makeQuery(id+"F0.imprint","IMPRINT",EDGE,{"derivedFrom":subQ0}),1.0]])]});}
            extrude(context, id + "F2", {"entities" : qUnion([Q0, Q1, Q2, Q3]), "depth" : 25.4 * mm});
        }
        {
            var Q0;
            {var subQ0=sQuery(id+"F0.wireOp",EDGE,"E122");Q0=makeQuery(id+"F0.imprint","IMPRINT",FACE,{"disambiguationData":[TD([[makeQuery(id+"F0.imprint","IMPRINT",EDGE,{"derivedFrom":subQ0}),-1.0]])]});}
            var Q1;
            {var subQ1=sQuery(id+"F0.wireOp",EDGE,"E123");Q1=makeQuery(id+"F0.imprint","IMPRINT",FACE,{"disambiguationData":[TD([[makeQuery(id+"F0.imprint","IMPRINT",EDGE,{"derivedFrom":subQ1}),-1.0]])]});}
            var Q2;
            {var subQ0=sQuery(id+"F0.wireOp",EDGE,"E124");Q2=makeQuery(id+"F0.imprint","IMPRINT",FACE,{"disambiguationData":[TD([[makeQuery(id+"F0.imprint","IMPRINT",EDGE,{"derivedFrom":subQ0}),-1.0]])]});}
            var Q3;
            {var subQ0=sQuery(id+"F0.wireOp",EDGE,"E125");Q3=makeQuery(id+"F0.imprint","IMPRINT",FACE,{"disambiguationData":[TD([[makeQuery(id+"F0.imprint","IMPRINT",EDGE,{"derivedFrom":subQ0}),-1.0]])]});}
            extrude(context, id + "F3", {"entities" : qUnion([Q0, Q1, Q2, Q3]), "operationType" : NewBodyOperationType.ADD, "depth" : 22.86 * mm});
        }
        {
            var Q0;
            {var subQ0=sQuery(id+"F0.wireOp",EDGE,"E126");Q0=makeQuery(id+"F0.imprint","IMPRINT",FACE,{"disambiguationData":[TD([[makeQuery(id+"F0.imprint","IMPRINT",EDGE,{"derivedFrom":subQ0}),-1.0]])]});}
            var Q1;
            {var subQ1=sQuery(id+"F0.wireOp",EDGE,"E127");Q1=makeQuery(id+"F0.imprint","IMPRINT",FACE,{"disambiguationData":[TD([[makeQuery(id+"F0.imprint","IMPRINT",EDGE,{"derivedFrom":subQ1}),-1.0]])]});}
            var Q2;
            {var subQ0=sQuery(id+"F0.wireOp",EDGE,"E128");Q2=makeQuery(id+"F0.imprint","IMPRINT",FACE,{"disambiguationData":[TD([[makeQuery(id+"F0.imprint","IMPRINT",EDGE,{"derivedFrom":subQ0}),-1.0]])]});}
            var Q3;
            {var subQ0=sQuery(id+"F0.wireOp",EDGE,"E133");Q3=makeQuery(id+"F0.imprint","IMPRINT",FACE,{"disambiguationData":[TD([[makeQuery(id+"F0.imprint","IMPRINT",EDGE,{"derivedFrom":subQ0}),1.0]])]});}
            extrude(context, id + "F4", {"entities" : qUnion([Q0, Q1, Q2, Q3]), "operationType" : NewBodyOperationType.ADD, "depth" : 17.78 * mm});
        }
        {
            var Q0;
            {var subQ3=sQuery(id+"F0.wireOp",EDGE,"E130");Q0=makeQuery(id+"F0.imprint","IMPRINT",FACE,{"disambiguationData":[TD([[makeQuery(id+"F0.imprint","IMPRINT",EDGE,{"derivedFrom":subQ3}),1.0]])]});}
            var Q1;
            {var subQ2=sQuery(id+"F0.wireOp",EDGE,"E131");Q1=makeQuery(id+"F0.imprint","IMPRINT",FACE,{"disambiguationData":[TD([[makeQuery(id+"F0.imprint","IMPRINT",EDGE,{"derivedFrom":subQ2}),-1.0]])]});}
            var Q2;
            {var subQ0=sQuery(id+"F0.wireOp",EDGE,"E132");Q2=makeQuery(id+"F0.imprint","IMPRINT",FACE,{"disambiguationData":[TD([[makeQuery(id+"F0.imprint","IMPRINT",EDGE,{"derivedFrom":subQ0}),1.0]])]});}
            var Q3;
            {var subQ0=sQuery(id+"F0.wireOp",EDGE,"E133");Q3=makeQuery(id+"F0.imprint","IMPRINT",FACE,{"disambiguationData":[TD([[makeQuery(id+"F0.imprint","IMPRINT",EDGE,{"derivedFrom":subQ0}),-1.0]])]});}
            extrude(context, id + "F5", {"entities" : qUnion([Q0, Q1, Q2, Q3]), "operationType" : NewBodyOperationType.ADD, "depth" : 15.24 * mm});
        }
        {
            var Q0;
            {var subQ0=sQuery(id+"F0.wireOp",EDGE,"E113");Q0=makeQuery(id+"F0.imprint","IMPRINT",FACE,{"disambiguationData":[TD([[makeQuery(id+"F0.imprint","IMPRINT",EDGE,{"derivedFrom":subQ0}),1.0]])]});}
            var Q1;
            {var subQ2=sQuery(id+"F0.wireOp",EDGE,"E114");Q1=makeQuery(id+"F0.imprint","IMPRINT",FACE,{"disambiguationData":[TD([[makeQuery(id+"F0.imprint","IMPRINT",EDGE,{"derivedFrom":subQ2}),1.0]])]});}
            var Q2;
            {var subQ2=sQuery(id+"F0.wireOp",EDGE,"E115");Q2=makeQuery(id+"F0.imprint","IMPRINT",FACE,{"disambiguationData":[TD([[makeQuery(id+"F0.imprint","IMPRINT",EDGE,{"derivedFrom":subQ2}),1.0]])]});}
            var Q3;
            {var subQ0=sQuery(id+"F0.wireOp",EDGE,"E116");Q3=makeQuery(id+"F0.imprint","IMPRINT",FACE,{"disambiguationData":[TD([[makeQuery(id+"F0.imprint","IMPRINT",EDGE,{"derivedFrom":subQ0}),1.0]])]});}
            extrude(context, id + "F6", {"entities" : qUnion([Q0, Q1, Q2, Q3]), "depth" : 12.7 * mm});
        }
        {
            var Q0;
            Q0=makeQuery(id+"F0.imprint","IMPRINT",FACE,{"disambiguationData":[TD([[makeQuery(id+"F0.imprint","IMPRINT",EDGE,{"derivedFrom":sQuery(id+"F0.wireOp",EDGE,"E139.bottom")}),-1.0]])]});
            var Q1;
            Q1=makeQuery(id+"F0.imprint","IMPRINT",FACE,{"disambiguationData":[TD([[makeQuery(id+"F0.imprint","IMPRINT",EDGE,{"derivedFrom":sQuery(id+"F0.wireOp",EDGE,"E140.bottom")}),-1.0]])]});
            var Q2;
            Q2=makeQuery(id+"F0.imprint","IMPRINT",FACE,{"disambiguationData":[TD([[makeQuery(id+"F0.imprint","IMPRINT",EDGE,{"derivedFrom":sQuery(id+"F0.wireOp",EDGE,"E141.bottom")}),-1.0]])]});
            var Q3;
            Q3=makeQuery(id+"F0.imprint","IMPRINT",FACE,{"disambiguationData":[TD([[makeQuery(id+"F0.imprint","IMPRINT",EDGE,{"derivedFrom":sQuery(id+"F0.wireOp",EDGE,"E144.bottom")}),-1.0]])]});
            var Q4;
            Q4=makeQuery(id+"F0.imprint","IMPRINT",FACE,{"disambiguationData":[TD([[makeQuery(id+"F0.imprint","IMPRINT",EDGE,{"derivedFrom":sQuery(id+"F0.wireOp",EDGE,"E143.bottom")}),-1.0]])]});
            var Q5;
            Q5=makeQuery(id+"F0.imprint","IMPRINT",FACE,{"disambiguationData":[TD([[makeQuery(id+"F0.imprint","IMPRINT",EDGE,{"derivedFrom":sQuery(id+"F0.wireOp",EDGE,"E142.bottom")}),-1.0]])]});
            var Q6;
            Q6=makeQuery(id+"F0.imprint","IMPRINT",FACE,{"disambiguationData":[TD([[makeQuery(id+"F0.imprint","IMPRINT",EDGE,{"derivedFrom":sQuery(id+"F0.wireOp",EDGE,"E117.bottom")}),-1.0]])]});
            var Q7;
            Q7=makeQuery(id+"F0.imprint","IMPRINT",FACE,{"disambiguationData":[TD([[makeQuery(id+"F0.imprint","IMPRINT",EDGE,{"derivedFrom":sQuery(id+"F0.wireOp",EDGE,"E145.bottom")}),-1.0]])]});
            var Q8;
            Q8=makeQuery(id+"F0.imprint","IMPRINT",FACE,{"disambiguationData":[TD([[makeQuery(id+"F0.imprint","IMPRINT",EDGE,{"derivedFrom":sQuery(id+"F0.wireOp",EDGE,"E118.bottom")}),-1.0]])]});
            extrude(context, id + "F7", {"entities" : qUnion([Q0, Q1, Q2, Q3, Q4, Q5, Q6, Q7, Q8]), "depth" : 12.7 * mm});
        }
        {
            var Q0;
            Q0=makeQuery(id+"F0.imprint","IMPRINT",FACE,{"disambiguationData":[TD([[makeQuery(id+"F0.imprint","IMPRINT",EDGE,{"derivedFrom":sQuery(id+"F0.wireOp",EDGE,"E104")}),1.0]])]});
            var Q1;
            Q1=makeQuery(id+"F0.imprint","IMPRINT",FACE,{"disambiguationData":[TD([[makeQuery(id+"F0.imprint","IMPRINT",EDGE,{"derivedFrom":sQuery(id+"F0.wireOp",EDGE,"E105")}),1.0]])]});
            var Q2;
            Q2=makeQuery(id+"F0.imprint","IMPRINT",FACE,{"disambiguationData":[TD([[makeQuery(id+"F0.imprint","IMPRINT",EDGE,{"derivedFrom":sQuery(id+"F0.wireOp",EDGE,"E112")}),1.0]])]});
            var Q3;
            Q3=makeQuery(id+"F0.imprint","IMPRINT",FACE,{"disambiguationData":[TD([[makeQuery(id+"F0.imprint","IMPRINT",EDGE,{"derivedFrom":sQuery(id+"F0.wireOp",EDGE,"E106")}),1.0]])]});
            var Q4;
            Q4=makeQuery(id+"F0.imprint","IMPRINT",FACE,{"disambiguationData":[TD([[makeQuery(id+"F0.imprint","IMPRINT",EDGE,{"derivedFrom":sQuery(id+"F0.wireOp",EDGE,"E107")}),1.0]])]});
            var Q5;
            Q5=makeQuery(id+"F0.imprint","IMPRINT",FACE,{"disambiguationData":[TD([[makeQuery(id+"F0.imprint","IMPRINT",EDGE,{"derivedFrom":sQuery(id+"F0.wireOp",EDGE,"E108")}),1.0]])]});
            var Q6;
            Q6=makeQuery(id+"F0.imprint","IMPRINT",FACE,{"disambiguationData":[TD([[makeQuery(id+"F0.imprint","IMPRINT",EDGE,{"derivedFrom":sQuery(id+"F0.wireOp",EDGE,"E109")}),1.0]])]});
            var Q7;
            Q7=makeQuery(id+"F0.imprint","IMPRINT",FACE,{"disambiguationData":[TD([[makeQuery(id+"F0.imprint","IMPRINT",EDGE,{"derivedFrom":sQuery(id+"F0.wireOp",EDGE,"E110")}),1.0]])]});
            extrude(context, id + "F8", {"entities" : qUnion([Q0, Q1, Q2, Q3, Q4, Q5, Q6, Q7]), "depth" : 12.7 * mm});
        }
        {
            var Q0;
            Q0=sQuery(id+"F0.wireOp",EDGE,"E1.top");
            var Q1;
            Q1=sQuery(id+"F0.wireOp",EDGE,"E33");
            var Q2;
            Q2=sQuery(id+"F0.wireOp",EDGE,"E10");
            var Q3;
            Q3=sQuery(id+"F0.wireOp",EDGE,"E31");
            var Q4;
            Q4=sQuery(id+"F0.wireOp",EDGE,"E7");
            var Q5;
            Q5=sQuery(id+"F0.wireOp",EDGE,"E29");
            var Q6;
            Q6=sQuery(id+"F0.wireOp",EDGE,"E6");
            var Q7;
            Q7=sQuery(id+"F0.wireOp",EDGE,"E27");
            var Q8;
            Q8=sQuery(id+"F0.wireOp",EDGE,"E9");
            var Q9;
            Q9=sQuery(id+"F0.wireOp",EDGE,"E26");
            var Q10;
            Q10=sQuery(id+"F0.wireOp",EDGE,"E8");
            var Q11;
            Q11=sQuery(id+"F0.wireOp",EDGE,"E23");
            var Q12;
            Q12=sQuery(id+"F0.wireOp",EDGE,"E1.bottom");
            extrude(context, id + "F9", {"bodyType" : ToolBodyType.SURFACE, "surfaceEntities" : qUnion([Q0, Q1, Q2, Q3, Q4, Q5, Q6, Q7, Q8, Q9, Q10, Q11, Q12]), "depth" : 12.7 * mm});
        }
        {
            var Q0;
            Q0=makeQuery(id+"F0.imprint","IMPRINT",FACE,{"disambiguationData":[TD([[makeQuery(id+"F0.imprint","IMPRINT",EDGE,{"derivedFrom":sQuery(id+"F0.wireOp",EDGE,"E192.bottom")}),-1.0]])]});
            extrude(context, id + "F10", {"entities" : qUnion([Q0]), "depth" : 25.4 * mm});
        }
        {
            var Q0;
            Q0=makeQuery(id+"F0.imprint","IMPRINT",FACE,{"disambiguationData":[TD([[makeQuery(id+"F0.imprint","IMPRINT",EDGE,{"derivedFrom":sQuery(id+"F0.wireOp",EDGE,"E193.bottom")}),-1.0]])]});
            extrude(context, id + "F11", {"entities" : qUnion([Q0]), "depth" : 25.4 * mm});
        }
        {
            var Q0;
            Q0=makeQuery(id+"F0.imprint","IMPRINT",FACE,{"disambiguationData":[TD([[makeQuery(id+"F0.imprint","IMPRINT",EDGE,{"derivedFrom":sQuery(id+"F0.wireOp",EDGE,"E194.bottom")}),-1.0]])]});
            extrude(context, id + "F12", {"entities" : qUnion([Q0]), "depth" : 25.4 * mm});
        }
        {
            var Q0;
            Q0=makeQuery(id+"F0.imprint","IMPRINT",FACE,{"disambiguationData":[TD([[makeQuery(id+"F0.imprint","IMPRINT",EDGE,{"derivedFrom":sQuery(id+"F0.wireOp",EDGE,"E195.bottom")}),-1.0]])]});
            extrude(context, id + "F13", {"entities" : qUnion([Q0]), "depth" : 25.4 * mm});
        }
        {
            var Q0;
            {var subQ0=sQuery(id+"F0.wireOp",EDGE,"E146.left");var subQ1=sQuery(id+"F0.wireOp",EDGE,"E146.top");var subQ2=makeQuery(id+"F0.imprint","INTERSECT",VERTEX,{"derivedFrom":[subQ1,subQ0]});Q0=makeQuery(id+"F0.imprint","IMPRINT",FACE,{"disambiguationData":[TD([[makeQuery(id+"F0.imprint","IMPRINT",EDGE,{"disambiguationData":[TD([[subQ2,-1.0]])],"derivedFrom":subQ1}),-1.0]])]});}
            var Q1;
            {var subQ0=sQuery(id+"F0.wireOp",EDGE,"E161");var subQ1=sQuery(id+"F0.wireOp",EDGE,"E146.left");var subQ2=makeQuery(id+"F0.imprint","INTERSECT",VERTEX,{"derivedFrom":[subQ1,subQ0]});Q1=makeQuery(id+"F0.imprint","IMPRINT",FACE,{"disambiguationData":[TD([[makeQuery(id+"F0.imprint","IMPRINT",EDGE,{"disambiguationData":[TD([[subQ2,-1.0]])],"derivedFrom":subQ1}),-1.0]])]});}
            var Q2;
            {var subQ0=sQuery(id+"F0.wireOp",EDGE,"E161");var subQ1=sQuery(id+"F0.wireOp",EDGE,"E146.left");var subQ2=makeQuery(id+"F0.imprint","INTERSECT",VERTEX,{"derivedFrom":[subQ1,subQ0]});Q2=makeQuery(id+"F0.imprint","IMPRINT",FACE,{"disambiguationData":[TD([[makeQuery(id+"F0.imprint","IMPRINT",EDGE,{"disambiguationData":[TD([[subQ2,1.0]])],"derivedFrom":subQ1}),-1.0]])]});}
            var Q3;
            {var subQ1=sQuery(id+"F0.wireOp",EDGE,"E1.left");var subQ3=sQuery(id+"F0.wireOp",EDGE,"E186");var subQ4=makeQuery(id+"F0.imprint","INTERSECT",VERTEX,{"derivedFrom":[subQ1,subQ3]});Q3=makeQuery(id+"F0.imprint","IMPRINT",FACE,{"disambiguationData":[TD([[makeQuery(id+"F0.imprint","IMPRINT",EDGE,{"disambiguationData":[TD([[subQ4,-1.0]])],"derivedFrom":subQ3}),1.0]])]});}
            var Q4;
            {var subQ0=sQuery(id+"F0.wireOp",EDGE,"E23");Q4=makeQuery(id+"F0.imprint","IMPRINT",FACE,{"disambiguationData":[TD([[makeQuery(id+"F0.imprint","IMPRINT",EDGE,{"derivedFrom":subQ0}),-1.0]])]});}
            var Q5;
            {var subQ0=sQuery(id+"F0.wireOp",EDGE,"E146.left");var subQ5=sQuery(id+"F0.wireOp",EDGE,"E173");var subQ6=makeQuery(id+"F0.imprint","INTERSECT",VERTEX,{"derivedFrom":[subQ0,subQ5]});Q5=makeQuery(id+"F0.imprint","IMPRINT",FACE,{"disambiguationData":[TD([[makeQuery(id+"F0.imprint","IMPRINT",EDGE,{"disambiguationData":[TD([[subQ6,1.0]])],"derivedFrom":subQ5}),1.0]])]});}
            var Q6;
            {var subQ0=sQuery(id+"F0.wireOp",EDGE,"E164");var subQ1=sQuery(id+"F0.wireOp",EDGE,"E146.top");var subQ2=makeQuery(id+"F0.imprint","INTERSECT",VERTEX,{"derivedFrom":[subQ1,subQ0]});Q6=makeQuery(id+"F0.imprint","IMPRINT",FACE,{"disambiguationData":[TD([[makeQuery(id+"F0.imprint","IMPRINT",EDGE,{"disambiguationData":[TD([[subQ2,1.0]])],"derivedFrom":subQ1}),-1.0]])]});}
            var Q7;
            {var subQ0=sQuery(id+"F0.wireOp",EDGE,"E164");var subQ1=sQuery(id+"F0.wireOp",EDGE,"E146.top");var subQ2=makeQuery(id+"F0.imprint","INTERSECT",VERTEX,{"derivedFrom":[subQ1,subQ0]});Q7=makeQuery(id+"F0.imprint","IMPRINT",FACE,{"disambiguationData":[TD([[makeQuery(id+"F0.imprint","IMPRINT",EDGE,{"disambiguationData":[TD([[subQ2,-1.0]])],"derivedFrom":subQ1}),-1.0]])]});}
            var Q8;
            {var subQ0=sQuery(id+"F0.wireOp",EDGE,"E157");var subQ1=sQuery(id+"F0.wireOp",EDGE,"E146.top");var subQ2=makeQuery(id+"F0.imprint","INTERSECT",VERTEX,{"derivedFrom":[subQ1,subQ0]});Q8=makeQuery(id+"F0.imprint","IMPRINT",FACE,{"disambiguationData":[TD([[makeQuery(id+"F0.imprint","IMPRINT",EDGE,{"disambiguationData":[TD([[subQ2,1.0]])],"derivedFrom":subQ1}),-1.0]])]});}
            var Q9;
            {var subQ0=sQuery(id+"F0.wireOp",EDGE,"E157");var subQ1=sQuery(id+"F0.wireOp",EDGE,"E146.top");var subQ2=makeQuery(id+"F0.imprint","INTERSECT",VERTEX,{"derivedFrom":[subQ1,subQ0]});Q9=makeQuery(id+"F0.imprint","IMPRINT",FACE,{"disambiguationData":[TD([[makeQuery(id+"F0.imprint","IMPRINT",EDGE,{"disambiguationData":[TD([[subQ2,-1.0]])],"derivedFrom":subQ1}),-1.0]])]});}
            var Q10;
            {var subQ0=sQuery(id+"F0.wireOp",EDGE,"E180");var subQ1=sQuery(id+"F0.wireOp",EDGE,"E146.top");var subQ2=makeQuery(id+"F0.imprint","INTERSECT",VERTEX,{"derivedFrom":[subQ1,subQ0]});Q10=makeQuery(id+"F0.imprint","IMPRINT",FACE,{"disambiguationData":[TD([[makeQuery(id+"F0.imprint","IMPRINT",EDGE,{"disambiguationData":[TD([[subQ2,1.0]])],"derivedFrom":subQ1}),-1.0]])]});}
            var Q11;
            {var subQ0=sQuery(id+"F0.wireOp",EDGE,"E161");var subQ5=sQuery(id+"F0.wireOp",EDGE,"E176");var subQ7=makeQuery(id+"F0.imprint","INTERSECT",VERTEX,{"derivedFrom":[subQ0,subQ5]});Q11=makeQuery(id+"F0.imprint","IMPRINT",FACE,{"disambiguationData":[TD([[makeQuery(id+"F0.imprint","IMPRINT",EDGE,{"disambiguationData":[TD([[subQ7,1.0]])],"derivedFrom":subQ5}),1.0]])]});}
            var Q12;
            {var subQ0=sQuery(id+"F0.wireOp",EDGE,"E164");var subQ1=sQuery(id+"F0.wireOp",EDGE,"E161");var subQ2=makeQuery(id+"F0.imprint","INTERSECT",VERTEX,{"derivedFrom":[subQ1,subQ0]});Q12=makeQuery(id+"F0.imprint","IMPRINT",FACE,{"disambiguationData":[TD([[makeQuery(id+"F0.imprint","IMPRINT",EDGE,{"disambiguationData":[TD([[subQ2,-1.0]])],"derivedFrom":subQ1}),1.0]])]});}
            var Q13;
            {var subQ0=sQuery(id+"F0.wireOp",EDGE,"E174");var subQ1=sQuery(id+"F0.wireOp",EDGE,"E161");var subQ2=makeQuery(id+"F0.imprint","INTERSECT",VERTEX,{"derivedFrom":[subQ1,subQ0]});Q13=makeQuery(id+"F0.imprint","IMPRINT",FACE,{"disambiguationData":[TD([[makeQuery(id+"F0.imprint","IMPRINT",EDGE,{"disambiguationData":[TD([[subQ2,-1.0]])],"derivedFrom":subQ1}),1.0]])]});}
            var Q14;
            {var subQ0=sQuery(id+"F0.wireOp",EDGE,"E174");var subQ1=sQuery(id+"F0.wireOp",EDGE,"E161");var subQ2=makeQuery(id+"F0.imprint","INTERSECT",VERTEX,{"derivedFrom":[subQ1,subQ0]});Q14=makeQuery(id+"F0.imprint","IMPRINT",FACE,{"disambiguationData":[TD([[makeQuery(id+"F0.imprint","IMPRINT",EDGE,{"disambiguationData":[TD([[subQ2,-1.0]])],"derivedFrom":subQ1}),-1.0]])]});}
            var Q15;
            {var subQ1=sQuery(id+"F0.wireOp",EDGE,"E146.bottom");var subQ3=sQuery(id+"F0.wireOp",EDGE,"E164");var subQ4=makeQuery(id+"F0.imprint","INTERSECT",VERTEX,{"derivedFrom":[subQ1,subQ3]});Q15=makeQuery(id+"F0.imprint","IMPRINT",FACE,{"disambiguationData":[TD([[makeQuery(id+"F0.imprint","IMPRINT",EDGE,{"disambiguationData":[TD([[subQ4,1.0]])],"derivedFrom":subQ3}),-1.0]])]});}
            extrude(context, id + "F14", {"entities" : qUnion([Q0, Q1, Q2, Q3, Q4, Q5, Q6, Q7, Q8, Q9, Q10, Q11, Q12, Q13, Q14, Q15]), "depth" : 25.4 * mm});
        }
        {
            var Q0;
            {var subQ0=sQuery(id+"F0.wireOp",EDGE,"E26");Q0=makeQuery(id+"F0.imprint","IMPRINT",FACE,{"disambiguationData":[TD([[makeQuery(id+"F0.imprint","IMPRINT",EDGE,{"derivedFrom":subQ0}),1.0]])]});}
            var Q1;
            {var subQ3=sQuery(id+"F0.wireOp",EDGE,"E188");Q1=makeQuery(id+"F0.imprint","IMPRINT",FACE,{"disambiguationData":[TD([[makeQuery(id+"F0.imprint","IMPRINT",EDGE,{"derivedFrom":subQ3}),1.0]])]});}
            var Q2;
            {var subQ0=sQuery(id+"F0.wireOp",EDGE,"E177");var subQ1=sQuery(id+"F0.wireOp",EDGE,"E8");var subQ2=makeQuery(id+"F0.imprint","INTERSECT",VERTEX,{"derivedFrom":[subQ1,subQ0]});Q2=makeQuery(id+"F0.imprint","IMPRINT",FACE,{"disambiguationData":[TD([[makeQuery(id+"F0.imprint","IMPRINT",EDGE,{"disambiguationData":[TD([[subQ2,-1.0]])],"derivedFrom":subQ1}),-1.0]])]});}
            var Q3;
            {var subQ3=sQuery(id+"F0.wireOp",EDGE,"E177");var subQ5=sQuery(id+"F0.wireOp",EDGE,"E187");var subQ6=makeQuery(id+"F0.imprint","INTERSECT",VERTEX,{"derivedFrom":[subQ3,subQ5]});Q3=makeQuery(id+"F0.imprint","IMPRINT",FACE,{"disambiguationData":[TD([[makeQuery(id+"F0.imprint","IMPRINT",EDGE,{"disambiguationData":[TD([[subQ6,1.0]])],"derivedFrom":subQ5}),1.0]])]});}
            var Q4;
            {var subQ1=sQuery(id+"F0.wireOp",EDGE,"E162");var subQ3=sQuery(id+"F0.wireOp",EDGE,"E176");var subQ4=makeQuery(id+"F0.imprint","INTERSECT",VERTEX,{"derivedFrom":[subQ1,subQ3]});Q4=makeQuery(id+"F0.imprint","IMPRINT",FACE,{"disambiguationData":[TD([[makeQuery(id+"F0.imprint","IMPRINT",EDGE,{"disambiguationData":[TD([[subQ4,1.0]])],"derivedFrom":subQ3}),-1.0]])]});}
            var Q5;
            {var subQ0=sQuery(id+"F0.wireOp",EDGE,"E164");var subQ1=sQuery(id+"F0.wireOp",EDGE,"E146.bottom");var subQ2=makeQuery(id+"F0.imprint","INTERSECT",VERTEX,{"derivedFrom":[subQ1,subQ0]});Q5=makeQuery(id+"F0.imprint","IMPRINT",FACE,{"disambiguationData":[TD([[makeQuery(id+"F0.imprint","IMPRINT",EDGE,{"disambiguationData":[TD([[subQ2,-1.0]])],"derivedFrom":subQ1}),-1.0]])]});}
            var Q6;
            {var subQ0=sQuery(id+"F0.wireOp",EDGE,"E182");var subQ1=sQuery(id+"F0.wireOp",EDGE,"E146.bottom");var subQ2=makeQuery(id+"F0.imprint","INTERSECT",VERTEX,{"derivedFrom":[subQ1,subQ0]});Q6=makeQuery(id+"F0.imprint","IMPRINT",FACE,{"disambiguationData":[TD([[makeQuery(id+"F0.imprint","IMPRINT",EDGE,{"disambiguationData":[TD([[subQ2,1.0]])],"derivedFrom":subQ1}),1.0]])]});}
            var Q7;
            {var subQ3=sQuery(id+"F0.wireOp",EDGE,"E191");Q7=makeQuery(id+"F0.imprint","IMPRINT",FACE,{"disambiguationData":[TD([[makeQuery(id+"F0.imprint","IMPRINT",EDGE,{"derivedFrom":subQ3}),-1.0]])]});}
            var Q8;
            {var subQ3=sQuery(id+"F0.wireOp",EDGE,"E182");var subQ5=sQuery(id+"F0.wireOp",EDGE,"E183");var subQ7=makeQuery(id+"F0.imprint","INTERSECT",VERTEX,{"derivedFrom":[subQ3,subQ5]});Q8=makeQuery(id+"F0.imprint","IMPRINT",FACE,{"disambiguationData":[TD([[makeQuery(id+"F0.imprint","IMPRINT",EDGE,{"disambiguationData":[TD([[subQ7,-1.0]])],"derivedFrom":subQ3}),1.0]])]});}
            var Q9;
            {var subQ0=sQuery(id+"F0.wireOp",EDGE,"E146.bottom");var subQ1=sQuery(id+"F0.wireOp",EDGE,"E1.right");var subQ2=makeQuery(id+"F0.imprint","INTERSECT",VERTEX,{"derivedFrom":[subQ1,subQ0]});Q9=makeQuery(id+"F0.imprint","IMPRINT",FACE,{"disambiguationData":[TD([[makeQuery(id+"F0.imprint","IMPRINT",EDGE,{"disambiguationData":[TD([[subQ2,-1.0]])],"derivedFrom":subQ1}),-1.0]])]});}
            var Q10;
            {var subQ0=sQuery(id+"F0.wireOp",EDGE,"E162");var subQ1=sQuery(id+"F0.wireOp",EDGE,"E1.right");var subQ2=makeQuery(id+"F0.imprint","INTERSECT",VERTEX,{"derivedFrom":[subQ1,subQ0]});Q10=makeQuery(id+"F0.imprint","IMPRINT",FACE,{"disambiguationData":[TD([[makeQuery(id+"F0.imprint","IMPRINT",EDGE,{"disambiguationData":[TD([[subQ2,1.0]])],"derivedFrom":subQ1}),-1.0]])]});}
            var Q11;
            {var subQ0=sQuery(id+"F0.wireOp",EDGE,"E191");Q11=makeQuery(id+"F0.imprint","IMPRINT",FACE,{"disambiguationData":[TD([[makeQuery(id+"F0.imprint","IMPRINT",EDGE,{"derivedFrom":subQ0}),1.0]])]});}
            var Q12;
            {var subQ0=sQuery(id+"F0.wireOp",EDGE,"E180");var subQ5=sQuery(id+"F0.wireOp",EDGE,"E179");var subQ7=makeQuery(id+"F0.imprint","INTERSECT",VERTEX,{"derivedFrom":[subQ5,subQ0]});Q12=makeQuery(id+"F0.imprint","IMPRINT",FACE,{"disambiguationData":[TD([[makeQuery(id+"F0.imprint","IMPRINT",EDGE,{"disambiguationData":[TD([[subQ7,-1.0]])],"derivedFrom":subQ5}),-1.0]])]});}
            var Q13;
            {var subQ0=sQuery(id+"F0.wireOp",EDGE,"E161");var subQ1=sQuery(id+"F0.wireOp",EDGE,"E160.1.0.0");var subQ2=makeQuery(id+"F0.imprint","INTERSECT",VERTEX,{"derivedFrom":[subQ1,subQ0]});Q13=makeQuery(id+"F0.imprint","IMPRINT",FACE,{"disambiguationData":[TD([[makeQuery(id+"F0.imprint","IMPRINT",EDGE,{"disambiguationData":[TD([[subQ2,1.0]])],"derivedFrom":subQ1}),-1.0]])]});}
            var Q14;
            {var subQ3=sQuery(id+"F0.wireOp",EDGE,"E189");Q14=makeQuery(id+"F0.imprint","IMPRINT",FACE,{"disambiguationData":[TD([[makeQuery(id+"F0.imprint","IMPRINT",EDGE,{"derivedFrom":subQ3}),-1.0]])]});}
            var Q15;
            {var subQ0=sQuery(id+"F0.wireOp",EDGE,"E184");Q15=makeQuery(id+"F0.imprint","IMPRINT",FACE,{"disambiguationData":[TD([[makeQuery(id+"F0.imprint","IMPRINT",EDGE,{"derivedFrom":subQ0}),1.0]])]});}
            extrude(context, id + "F15", {"entities" : qUnion([Q0, Q1, Q2, Q3, Q4, Q5, Q6, Q7, Q8, Q9, Q10, Q11, Q12, Q13, Q14, Q15]), "depth" : 12.7 * mm});
        }
        {
            var Q0;
            {var subQ1=sQuery(id+"F0.wireOp",EDGE,"E8");var subQ3=sQuery(id+"F0.wireOp",EDGE,"E178");var subQ4=makeQuery(id+"F0.imprint","INTERSECT",VERTEX,{"derivedFrom":[subQ1,subQ3]});Q0=makeQuery(id+"F0.imprint","IMPRINT",FACE,{"disambiguationData":[TD([[makeQuery(id+"F0.imprint","IMPRINT",EDGE,{"disambiguationData":[TD([[subQ4,1.0]])],"derivedFrom":subQ3}),-1.0]])]});}
            var Q1;
            {var subQ0=sQuery(id+"F0.wireOp",EDGE,"E23");Q1=makeQuery(id+"F0.imprint","IMPRINT",FACE,{"disambiguationData":[TD([[makeQuery(id+"F0.imprint","IMPRINT",EDGE,{"derivedFrom":subQ0}),1.0]])]});}
            var Q2;
            {var subQ3=sQuery(id+"F0.wireOp",EDGE,"E164");var subQ5=sQuery(id+"F0.wireOp",EDGE,"E186");var subQ6=makeQuery(id+"F0.imprint","INTERSECT",VERTEX,{"derivedFrom":[subQ3,subQ5]});Q2=makeQuery(id+"F0.imprint","IMPRINT",FACE,{"disambiguationData":[TD([[makeQuery(id+"F0.imprint","IMPRINT",EDGE,{"disambiguationData":[TD([[subQ6,1.0]])],"derivedFrom":subQ5}),-1.0]])]});}
            var Q3;
            {var subQ1=sQuery(id+"F0.wireOp",EDGE,"E146.bottom");var subQ3=sQuery(id+"F0.wireOp",EDGE,"E164");var subQ4=makeQuery(id+"F0.imprint","INTERSECT",VERTEX,{"derivedFrom":[subQ1,subQ3]});Q3=makeQuery(id+"F0.imprint","IMPRINT",FACE,{"disambiguationData":[TD([[makeQuery(id+"F0.imprint","IMPRINT",EDGE,{"disambiguationData":[TD([[subQ4,-1.0]])],"derivedFrom":subQ3}),-1.0]])]});}
            var Q4;
            {var subQ0=sQuery(id+"F0.wireOp",EDGE,"E164");var subQ1=sQuery(id+"F0.wireOp",EDGE,"E146.bottom");var subQ2=makeQuery(id+"F0.imprint","INTERSECT",VERTEX,{"derivedFrom":[subQ1,subQ0]});Q4=makeQuery(id+"F0.imprint","IMPRINT",FACE,{"disambiguationData":[TD([[makeQuery(id+"F0.imprint","IMPRINT",EDGE,{"disambiguationData":[TD([[subQ2,-1.0]])],"derivedFrom":subQ1}),1.0]])]});}
            var Q5;
            {var subQ3=sQuery(id+"F0.wireOp",EDGE,"E146.bottom");var subQ5=makeQuery(id+"F0.imprint","INTERSECT",VERTEX,{"derivedFrom":[sQuery(id+"F0.wireOp",EDGE,"E1.right"),subQ3]});Q5=makeQuery(id+"F0.imprint","IMPRINT",FACE,{"disambiguationData":[TD([[makeQuery(id+"F0.imprint","IMPRINT",EDGE,{"disambiguationData":[TD([[subQ5,1.0]])],"derivedFrom":subQ3}),1.0]])]});}
            var Q6;
            {var subQ0=sQuery(id+"F0.wireOp",EDGE,"E164");var subQ1=sQuery(id+"F0.wireOp",EDGE,"E161");var subQ2=makeQuery(id+"F0.imprint","INTERSECT",VERTEX,{"derivedFrom":[subQ1,subQ0]});Q6=makeQuery(id+"F0.imprint","IMPRINT",FACE,{"disambiguationData":[TD([[makeQuery(id+"F0.imprint","IMPRINT",EDGE,{"disambiguationData":[TD([[subQ2,-1.0]])],"derivedFrom":subQ1}),-1.0]])]});}
            var Q7;
            {var subQ1=sQuery(id+"F0.wireOp",EDGE,"E161");var subQ3=sQuery(id+"F0.wireOp",EDGE,"E176");var subQ4=makeQuery(id+"F0.imprint","INTERSECT",VERTEX,{"derivedFrom":[subQ1,subQ3]});Q7=makeQuery(id+"F0.imprint","IMPRINT",FACE,{"disambiguationData":[TD([[makeQuery(id+"F0.imprint","IMPRINT",EDGE,{"disambiguationData":[TD([[subQ4,-1.0]])],"derivedFrom":subQ3}),1.0]])]});}
            var Q8;
            {var subQ3=sQuery(id+"F0.wireOp",EDGE,"E179");var subQ5=sQuery(id+"F0.wireOp",EDGE,"E181");var subQ7=makeQuery(id+"F0.imprint","INTERSECT",VERTEX,{"derivedFrom":[subQ3,subQ5]});Q8=makeQuery(id+"F0.imprint","IMPRINT",FACE,{"disambiguationData":[TD([[makeQuery(id+"F0.imprint","IMPRINT",EDGE,{"disambiguationData":[TD([[subQ7,1.0]])],"derivedFrom":subQ3}),-1.0]])]});}
            var Q9;
            {var subQ3=sQuery(id+"F0.wireOp",EDGE,"E181");var subQ5=sQuery(id+"F0.wireOp",EDGE,"E179");var subQ6=makeQuery(id+"F0.imprint","INTERSECT",VERTEX,{"derivedFrom":[subQ5,subQ3]});Q9=makeQuery(id+"F0.imprint","IMPRINT",FACE,{"disambiguationData":[TD([[makeQuery(id+"F0.imprint","IMPRINT",EDGE,{"disambiguationData":[TD([[subQ6,-1.0]])],"derivedFrom":subQ5}),-1.0]])]});}
            var Q10;
            {var subQ0=sQuery(id+"F0.wireOp",EDGE,"E180");var subQ1=sQuery(id+"F0.wireOp",EDGE,"E146.top");var subQ2=makeQuery(id+"F0.imprint","INTERSECT",VERTEX,{"derivedFrom":[subQ1,subQ0]});Q10=makeQuery(id+"F0.imprint","IMPRINT",FACE,{"disambiguationData":[TD([[makeQuery(id+"F0.imprint","IMPRINT",EDGE,{"disambiguationData":[TD([[subQ2,-1.0]])],"derivedFrom":subQ1}),-1.0]])]});}
            var Q11;
            {var subQ0=sQuery(id+"F0.wireOp",EDGE,"E160.1.0.0");var subQ1=sQuery(id+"F0.wireOp",EDGE,"E146.top");var subQ2=makeQuery(id+"F0.imprint","INTERSECT",VERTEX,{"derivedFrom":[subQ1,subQ0]});Q11=makeQuery(id+"F0.imprint","IMPRINT",FACE,{"disambiguationData":[TD([[makeQuery(id+"F0.imprint","IMPRINT",EDGE,{"disambiguationData":[TD([[subQ2,1.0]])],"derivedFrom":subQ1}),-1.0]])]});}
            extrude(context, id + "F16", {"entities" : qUnion([Q0, Q1, Q2, Q3, Q4, Q5, Q6, Q7, Q8, Q9, Q10, Q11]), "depth" : 19.05 * mm});
        }
    });
